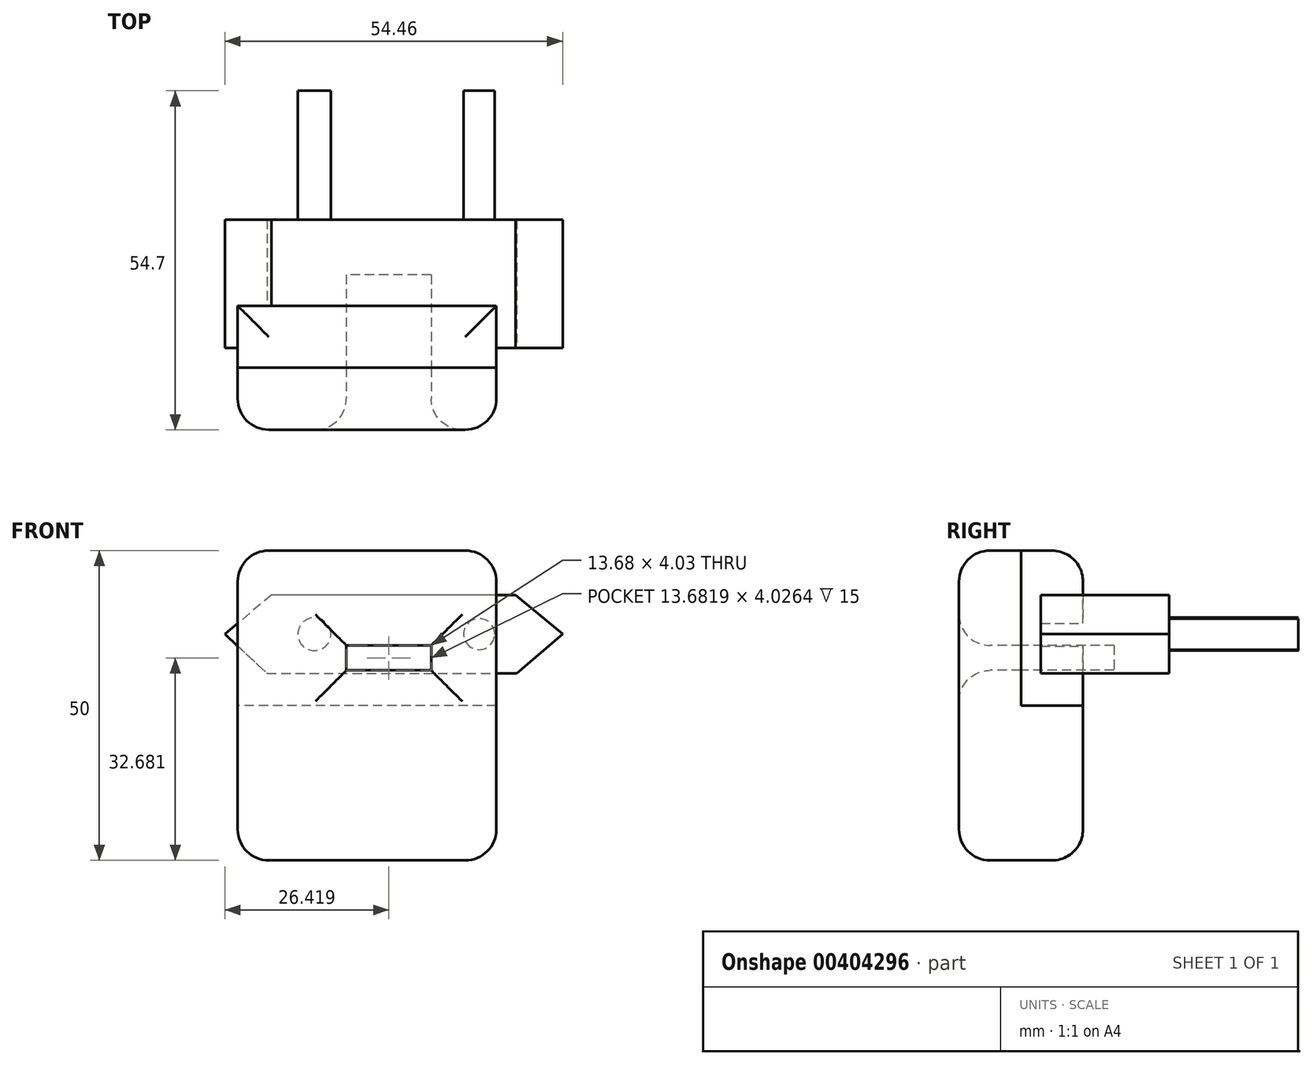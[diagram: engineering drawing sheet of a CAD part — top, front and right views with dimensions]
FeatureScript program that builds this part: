
annotation { "Feature Type Name" : "Feature", "Feature Type Description" : "" }
export const myFeature = defineFeature(function(context is Context, id is Id, definition is map)
    precondition{}
    {
        {
            var Q0;
            Q0=qCreatedBy(makeId("Right.planeOp"),FACE);
            var sketch = newSketch(context, id + "F0", { "sketchPlane" : qUnion([Q0])});
            skLineSegment(sketch, "E0.bottom", {"start": v(-10, -25) * mm, "end": v(10, -25) * mm});
            skLineSegment(sketch, "E0.top", {"start": v(-10, 25) * mm, "end": v(10, 25) * mm});
            skLineSegment(sketch, "E0.left", {"start": v(-10, -25) * mm, "end": v(-10, 25) * mm});
            skLineSegment(sketch, "E0.right", {"start": v(10, -25) * mm, "end": v(10, 25) * mm});
            skPoint(sketch, "E0.middle", {"position": v(0, 0) * mm});
            skSolve(sketch);
        }
        {
            var Q0;
            Q0 = qSketchRegion(id + "F0", true);
            extrude(context, id + "F1", {"entities" : qUnion([Q0]), "depth" : 41.7 * mm});
        }
        {
            var Q0;
            Q0=makeQuery(id+"F1.opExtrude","SWEPT_FACE",FACE,{"disambiguationData":[OSD([sQuery(id+"F0.wireOp",EDGE,"E0.right")])]});
            var sketch = newSketch(context, id + "F2", { "sketchPlane" : qUnion([Q0])});
            skLineSegment(sketch, "E1", {"start": v(-5.42, 17.86) * mm, "end": v(2.06, 11.52) * mm});
            skLineSegment(sketch, "E2", {"start": v(2.06, 11.52) * mm, "end": v(-4.72, 5.19) * mm});
            skLineSegment(sketch, "E3", {"start": v(-4.72, 5.19) * mm, "end": v(-45, 5.19) * mm});
            skLineSegment(sketch, "E4", {"start": v(-45, 5.19) * mm, "end": v(-52.4, 11.52) * mm});
            skLineSegment(sketch, "E5", {"start": v(-52.4, 11.52) * mm, "end": v(-44.83, 17.86) * mm});
            skLineSegment(sketch, "E6", {"start": v(-44.83, 17.86) * mm, "end": v(-5.42, 17.86) * mm});
            skSolve(sketch);
        }
        {
            var Q0;
            Q0 = qSketchRegion(id + "F2", true);
            extrude(context, id + "F3", {"entities" : qUnion([Q0]), "operationType" : NewBodyOperationType.ADD, "depth" : 13.9 * mm});
        }
        {
            var Q0;
            Q0=makeQuery(id+"F3.opExtrude","CAP_FACE",FACE,{"disambiguationData":[OSD([sQuery(id+"F2.wireOp",EDGE,"E1"),sQuery(id+"F2.wireOp",EDGE,"E2"),sQuery(id+"F2.wireOp",EDGE,"E3"),sQuery(id+"F2.wireOp",EDGE,"E4"),sQuery(id+"F2.wireOp",EDGE,"E5"),sQuery(id+"F2.wireOp",EDGE,"E6")])],"isStart":false});
            var sketch = newSketch(context, id + "F4", { "sketchPlane" : qUnion([Q0])});
            skCircle(sketch, "E7", {"center": v(-38.93, 11.52) * mm, "radius": 2.5 * mm});
            skCircle(sketch, "E8", {"center": v(-12.36, 11.52) * mm, "radius": 2.66 * mm});
            skSolve(sketch);
        }
        {
            var Q0;
            Q0 = qSketchRegion(id + "F4", true);
            extrude(context, id + "F5", {"entities" : qUnion([Q0]), "operationType" : NewBodyOperationType.ADD, "depth" : 20.8 * mm});
        }
        {
            var Q0;
            Q0=makeQuery(id+"F1.opExtrude","SWEPT_FACE",FACE,{"disambiguationData":[OSD([sQuery(id+"F0.wireOp",EDGE,"E0.left")])]});
            var sketch = newSketch(context, id + "F6", { "sketchPlane" : qUnion([Q0])});
            skLineSegment(sketch, "E9.bottom", {"start": v(31.2, 9.7) * mm, "end": v(17.52, 9.7) * mm});
            skLineSegment(sketch, "E9.top", {"start": v(31.2, 5.67) * mm, "end": v(17.52, 5.67) * mm});
            skLineSegment(sketch, "E9.left", {"start": v(31.2, 9.7) * mm, "end": v(31.2, 5.67) * mm});
            skLineSegment(sketch, "E9.right", {"start": v(17.52, 9.7) * mm, "end": v(17.52, 5.67) * mm});
            skPoint(sketch, "E9.middle", {"position": v(24.36, 7.68) * mm});
            skSolve(sketch);
        }
        {
            var Q0;
            Q0 = qSketchRegion(id + "F6", true);
            extrude(context, id + "F7", {"entities" : qUnion([Q0]), "operationType" : NewBodyOperationType.REMOVE, "oppositeDirection" : true, "depth" : 25 * mm});
        }
        {
            var Q0;
            Q0=makeQuery(id+"F1.opExtrude","SWEPT_FACE",FACE,{"disambiguationData":[OSD([sQuery(id+"F0.wireOp",EDGE,"E0.left")])]});
            var Q1;
            Q1=makeQuery(id+"F1.opExtrude","SWEPT_FACE",FACE,{"disambiguationData":[OSD([sQuery(id+"F0.wireOp",EDGE,"E0.bottom")])]});
            var Q2;
            Q2=makeQuery(id+"F1.opExtrude","SWEPT_FACE",FACE,{"disambiguationData":[OSD([sQuery(id+"F0.wireOp",EDGE,"E0.top")])]});
            fillet(context, id + "F8", {"entities" : qUnion([Q0, Q1, Q2]), "radius" : 5 * mm, "tangentPropagation" : true, "allowEdgeOverflow" : false});
        }
        {
            var Q0;
            {var subQ1=sQuery(id+"F2.wireOp",EDGE,"E4");var subQ2=sQuery(id+"F2.wireOp",EDGE,"E5");Q0=makeQuery(id+"F3.boolean.opBoolean","SPLIT",FACE,{"disambiguationData":[TD([makeQuery(id+"F3.opExtrude","SWEPT_FACE",FACE,{"disambiguationData":[OSD([subQ1])]})])],"derivedFrom":makeQuery(id+"F3.opExtrude","CAP_FACE",FACE,{"disambiguationData":[OSD([sQuery(id+"F2.wireOp",EDGE,"E1"),sQuery(id+"F2.wireOp",EDGE,"E2"),sQuery(id+"F2.wireOp",EDGE,"E3"),subQ1,subQ2,sQuery(id+"F2.wireOp",EDGE,"E6")])],"isStart":true})});}
            var Q1;
            {var subQ1=sQuery(id+"F2.wireOp",EDGE,"E2");var subQ2=sQuery(id+"F2.wireOp",EDGE,"E1");Q1=makeQuery(id+"F3.boolean.opBoolean","SPLIT",FACE,{"disambiguationData":[TD([makeQuery(id+"F3.opExtrude","SWEPT_FACE",FACE,{"disambiguationData":[OSD([subQ2])]})])],"derivedFrom":makeQuery(id+"F3.opExtrude","CAP_FACE",FACE,{"disambiguationData":[OSD([subQ2,subQ1,sQuery(id+"F2.wireOp",EDGE,"E3"),sQuery(id+"F2.wireOp",EDGE,"E4"),sQuery(id+"F2.wireOp",EDGE,"E5"),sQuery(id+"F2.wireOp",EDGE,"E6")])],"isStart":true})});}
            extrude(context, id + "F9", {"entities" : qUnion([Q0, Q1]), "operationType" : NewBodyOperationType.ADD, "depth" : 6.8 * mm});
        }
        {
            var Q0;
            Q0=makeQuery(id+"F1.opExtrude","CAP_FACE",FACE,{"disambiguationData":[OSD([sQuery(id+"F0.wireOp",EDGE,"E0.bottom"),sQuery(id+"F0.wireOp",EDGE,"E0.top"),sQuery(id+"F0.wireOp",EDGE,"E0.left"),sQuery(id+"F0.wireOp",EDGE,"E0.right")])],"isStart":false});
            var sketch = newSketch(context, id + "F10", { "sketchPlane" : qUnion([Q0])});
            skLineSegment(sketch, "E10.bottom", {"start": v(89.12, 31.74) * mm, "end": v(0, 31.74) * mm});
            skLineSegment(sketch, "E10.top", {"start": v(89.12, 0) * mm, "end": v(0, 0) * mm});
            skLineSegment(sketch, "E10.left", {"start": v(89.12, 31.74) * mm, "end": v(89.12, 0) * mm});
            skLineSegment(sketch, "E10.right", {"start": v(0, 31.74) * mm, "end": v(0, 0) * mm});
            skSolve(sketch);
        }
        {
            var Q0;
            Q0 = qSketchRegion(id + "F10", true);
            extrude(context, id + "F11", {"entities" : qUnion([Q0]), "oppositeDirection" : true, "depth" : 102.9 * mm, "hasSecondDirection" : true, "secondDirectionOppositeDirection" : false, "secondDirectionDepth" : 95.7 * mm});
        }
        {
            var Q0;
            Q0=makeQuery(id+"F11.opExtrude","SWEPT_BODY",BODY,{"disambiguationData":[OSD([sQuery(id+"F10.wireOp",EDGE,"E10.bottom"),sQuery(id+"F10.wireOp",EDGE,"E10.top"),sQuery(id+"F10.wireOp",EDGE,"E10.left"),sQuery(id+"F10.wireOp",EDGE,"E10.right")])]});
            transform(context, id + "F12", {"entities" : qUnion([Q0]), "transformType" : TransformType.TRANSLATION_3D, "dx" : 0 * mm, "dy" : 0 * mm, "dz" : 0 * mm, "makeCopy" : true});
        }
        {
            var Q0;
            Q0=makeQuery(id+"F1.opExtrude","SWEPT_BODY",BODY,{"disambiguationData":[OSD([sQuery(id+"F0.wireOp",EDGE,"E0.bottom"),sQuery(id+"F0.wireOp",EDGE,"E0.top"),sQuery(id+"F0.wireOp",EDGE,"E0.left"),sQuery(id+"F0.wireOp",EDGE,"E0.right")])]});
            transform(context, id + "F13", {"entities" : qUnion([Q0]), "transformType" : TransformType.TRANSLATION_3D, "dx" : 0 * mm, "dy" : 0 * mm, "dz" : 0 * mm, "makeCopy" : true});
        }
        {
            var Q0;
            Q0=makeQuery(id+"F11.opExtrude","SWEPT_BODY",BODY,{"disambiguationData":[OSD([sQuery(id+"F10.wireOp",EDGE,"E10.bottom"),sQuery(id+"F10.wireOp",EDGE,"E10.top"),sQuery(id+"F10.wireOp",EDGE,"E10.left"),sQuery(id+"F10.wireOp",EDGE,"E10.right")])]});
            var Q1;
            Q1=makeQuery(id+"F1.opExtrude","SWEPT_BODY",BODY,{"disambiguationData":[OSD([sQuery(id+"F0.wireOp",EDGE,"E0.bottom"),sQuery(id+"F0.wireOp",EDGE,"E0.top"),sQuery(id+"F0.wireOp",EDGE,"E0.left"),sQuery(id+"F0.wireOp",EDGE,"E0.right")])]});
            booleanBodies(context, id + "F14", {"operationType" : BooleanOperationType.SUBTRACTION, "tools" : qUnion([Q0]), "targets" : qUnion([Q1])});
        }
        {
            var Q0;
            Q0=makeQuery(id+"F13.opPattern","COPY",BODY,{"derivedFrom":makeQuery(id+"F1.opExtrude","SWEPT_BODY",BODY,{"disambiguationData":[OSD([sQuery(id+"F0.wireOp",EDGE,"E0.bottom"),sQuery(id+"F0.wireOp",EDGE,"E0.top"),sQuery(id+"F0.wireOp",EDGE,"E0.left"),sQuery(id+"F0.wireOp",EDGE,"E0.right")])]}),"instanceName":"1"});
            var Q1;
            Q1=makeQuery(id+"F12.opPattern","COPY",BODY,{"derivedFrom":makeQuery(id+"F11.opExtrude","SWEPT_BODY",BODY,{"disambiguationData":[OSD([sQuery(id+"F10.wireOp",EDGE,"E10.bottom"),sQuery(id+"F10.wireOp",EDGE,"E10.top"),sQuery(id+"F10.wireOp",EDGE,"E10.left"),sQuery(id+"F10.wireOp",EDGE,"E10.right")])]}),"instanceName":"1"});
            booleanBodies(context, id + "F15", {"operationType" : BooleanOperationType.INTERSECTION, "tools" : qUnion([Q0, Q1])});
        }
    });
